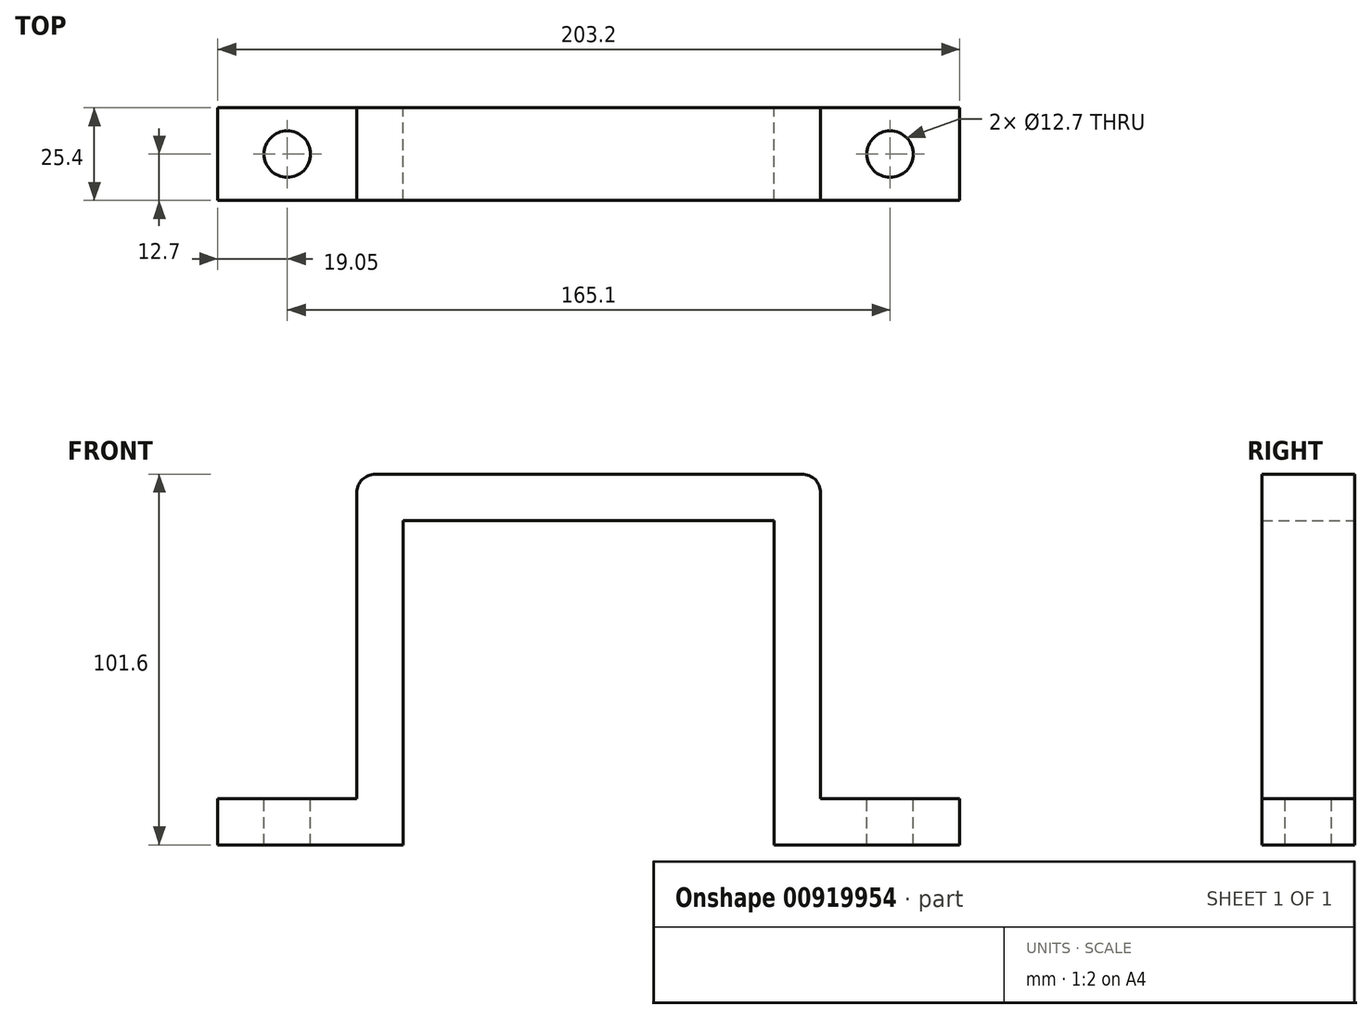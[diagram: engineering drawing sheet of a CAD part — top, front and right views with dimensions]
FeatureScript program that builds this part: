
annotation { "Feature Type Name" : "Feature", "Feature Type Description" : "" }
export const myFeature = defineFeature(function(context is Context, id is Id, definition is map)
    precondition{}
    {
        {
            var Q0;
            Q0=qCreatedBy(makeId("Top.planeOp"),FACE);
            var sketch = newSketch(context, id + "F0", { "sketchPlane" : qUnion([Q0])});
            skLineSegment(sketch, "E0.bottom", {"start": v(-63.5, 12.7) * mm, "end": v(63.5, 12.7) * mm});
            skLineSegment(sketch, "E0.top", {"start": v(-63.5, -12.7) * mm, "end": v(63.5, -12.7) * mm});
            skLineSegment(sketch, "E0.left", {"start": v(-63.5, 12.7) * mm, "end": v(-63.5, -12.7) * mm});
            skLineSegment(sketch, "E0.right", {"start": v(63.5, 12.7) * mm, "end": v(63.5, -12.7) * mm});
            skPoint(sketch, "E0.middle", {"position": v(0, 0) * mm});
            skSolve(sketch);
        }
        {
            var Q0;
            Q0 = qSketchRegion(id + "F0", true);
            extrude(context, id + "F1", {"entities" : qUnion([Q0]), "depth" : 12.7 * mm, "offsetDistance" : 25.4 * mm});
        }
        {
            var Q0;
            Q0=makeQuery(id+"F1.opExtrude","CAP_FACE",FACE,{"disambiguationData":[OSD([sQuery(id+"F0.wireOp",EDGE,"E0.bottom"),sQuery(id+"F0.wireOp",EDGE,"E0.top"),sQuery(id+"F0.wireOp",EDGE,"E0.left"),sQuery(id+"F0.wireOp",EDGE,"E0.right")])],"isStart":true});
            var sketch = newSketch(context, id + "F2", { "sketchPlane" : qUnion([Q0])});
            skLineSegment(sketch, "E1.bottom", {"start": v(63.5, 12.7) * mm, "end": v(50.8, 12.7) * mm});
            skLineSegment(sketch, "E1.top", {"start": v(63.5, -12.7) * mm, "end": v(50.8, -12.7) * mm});
            skLineSegment(sketch, "E1.left", {"start": v(63.5, 12.7) * mm, "end": v(63.5, -12.7) * mm});
            skLineSegment(sketch, "E1.right", {"start": v(50.8, 12.7) * mm, "end": v(50.8, -12.7) * mm});
            skSolve(sketch);
        }
        {
            var Q0;
            Q0 = qSketchRegion(id + "F2", true);
            extrude(context, id + "F3", {"entities" : qUnion([Q0]), "operationType" : NewBodyOperationType.ADD, "depth" : 76.2 * mm, "offsetDistance" : 25.4 * mm});
        }
        {
            var Q0;
            Q0=makeQuery(id+"F1.opExtrude","CAP_FACE",FACE,{"disambiguationData":[OSD([sQuery(id+"F0.wireOp",EDGE,"E0.bottom"),sQuery(id+"F0.wireOp",EDGE,"E0.top"),sQuery(id+"F0.wireOp",EDGE,"E0.left"),sQuery(id+"F0.wireOp",EDGE,"E0.right")])],"isStart":true});
            var sketch = newSketch(context, id + "F4", { "sketchPlane" : qUnion([Q0])});
            skLineSegment(sketch, "E2.bottom", {"start": v(-63.5, 12.7) * mm, "end": v(-50.8, 12.7) * mm});
            skLineSegment(sketch, "E2.top", {"start": v(-63.5, -12.7) * mm, "end": v(-50.8, -12.7) * mm});
            skLineSegment(sketch, "E2.left", {"start": v(-63.5, 12.7) * mm, "end": v(-63.5, -12.7) * mm});
            skLineSegment(sketch, "E2.right", {"start": v(-50.8, 12.7) * mm, "end": v(-50.8, -12.7) * mm});
            skSolve(sketch);
        }
        {
            var Q0;
            Q0 = qSketchRegion(id + "F4", true);
            extrude(context, id + "F5", {"entities" : qUnion([Q0]), "operationType" : NewBodyOperationType.ADD, "depth" : 76.2 * mm, "offsetDistance" : 25.4 * mm});
        }
        {
            var Q0;
            Q0=makeQuery(id+"F5.opExtrude","CAP_FACE",FACE,{"disambiguationData":[OSD([sQuery(id+"F4.wireOp",EDGE,"E2.bottom"),sQuery(id+"F4.wireOp",EDGE,"E2.top"),sQuery(id+"F4.wireOp",EDGE,"E2.left"),sQuery(id+"F4.wireOp",EDGE,"E2.right")])],"isStart":false});
            var sketch = newSketch(context, id + "F6", { "sketchPlane" : qUnion([Q0])});
            skLineSegment(sketch, "E3.bottom", {"start": v(-50.8, 12.7) * mm, "end": v(-101.6, 12.7) * mm});
            skLineSegment(sketch, "E3.top", {"start": v(-50.8, -12.7) * mm, "end": v(-101.6, -12.7) * mm});
            skLineSegment(sketch, "E3.left", {"start": v(-50.8, 12.7) * mm, "end": v(-50.8, -12.7) * mm});
            skLineSegment(sketch, "E3.right", {"start": v(-101.6, 12.7) * mm, "end": v(-101.6, -12.7) * mm});
            skSolve(sketch);
        }
        {
            var Q0;
            Q0 = qSketchRegion(id + "F6", true);
            extrude(context, id + "F7", {"entities" : qUnion([Q0]), "operationType" : NewBodyOperationType.ADD, "depth" : 12.7 * mm, "offsetDistance" : 25.4 * mm});
        }
        {
            var Q0;
            Q0=makeQuery(id+"F3.opExtrude","CAP_FACE",FACE,{"disambiguationData":[OSD([sQuery(id+"F2.wireOp",EDGE,"E1.bottom"),sQuery(id+"F2.wireOp",EDGE,"E1.top"),sQuery(id+"F2.wireOp",EDGE,"E1.left"),sQuery(id+"F2.wireOp",EDGE,"E1.right")])],"isStart":false});
            var sketch = newSketch(context, id + "F8", { "sketchPlane" : qUnion([Q0])});
            skLineSegment(sketch, "E4.bottom", {"start": v(50.8, 12.7) * mm, "end": v(101.6, 12.7) * mm});
            skLineSegment(sketch, "E4.top", {"start": v(50.8, -12.7) * mm, "end": v(101.6, -12.7) * mm});
            skLineSegment(sketch, "E4.left", {"start": v(50.8, 12.7) * mm, "end": v(50.8, -12.7) * mm});
            skLineSegment(sketch, "E4.right", {"start": v(101.6, 12.7) * mm, "end": v(101.6, -12.7) * mm});
            skSolve(sketch);
        }
        {
            var Q0;
            Q0 = qSketchRegion(id + "F8", true);
            extrude(context, id + "F9", {"entities" : qUnion([Q0]), "operationType" : NewBodyOperationType.ADD, "depth" : 12.7 * mm, "offsetDistance" : 25.4 * mm});
        }
        {
            var Q0;
            Q0=makeQuery(id+"F9.opExtrude","CAP_FACE",FACE,{"disambiguationData":[OSD([sQuery(id+"F8.wireOp",EDGE,"E4.bottom"),sQuery(id+"F8.wireOp",EDGE,"E4.top"),sQuery(id+"F8.wireOp",EDGE,"E4.left"),sQuery(id+"F8.wireOp",EDGE,"E4.right")])],"isStart":true});
            var sketch = newSketch(context, id + "F10", { "sketchPlane" : qUnion([Q0])});
            skLineSegment(sketch, "E5", {"start": v(101.6, 0) * mm, "end": v(63.5, 0) * mm});
            skCircle(sketch, "E6", {"center": v(82.55, 0) * mm, "radius": 6.35 * mm});
            skSolve(sketch);
        }
        {
            var Q0;
            Q0 = qSketchRegion(id + "F10", true);
            extrude(context, id + "F11", {"entities" : qUnion([Q0]), "operationType" : NewBodyOperationType.REMOVE, "oppositeDirection" : true, "depth" : 25.4 * mm, "offsetDistance" : 25.4 * mm});
        }
        {
            var Q0;
            Q0=makeQuery(id+"F7.opExtrude","CAP_FACE",FACE,{"disambiguationData":[OSD([sQuery(id+"F6.wireOp",EDGE,"E3.bottom"),sQuery(id+"F6.wireOp",EDGE,"E3.top"),sQuery(id+"F6.wireOp",EDGE,"E3.left"),sQuery(id+"F6.wireOp",EDGE,"E3.right")])],"isStart":true});
            var sketch = newSketch(context, id + "F12", { "sketchPlane" : qUnion([Q0])});
            skLineSegment(sketch, "E7", {"start": v(-101.6, 0) * mm, "end": v(-63.5, 0) * mm});
            skCircle(sketch, "E8", {"center": v(-82.55, 0) * mm, "radius": 6.35 * mm});
            skSolve(sketch);
        }
        {
            var Q0;
            Q0 = qSketchRegion(id + "F12", true);
            extrude(context, id + "F13", {"entities" : qUnion([Q0]), "operationType" : NewBodyOperationType.REMOVE, "oppositeDirection" : true, "depth" : 25.4 * mm, "offsetDistance" : 25.4 * mm});
        }
        {
            var Q0;
            Q0=makeQuery(id+"F1.opExtrude","CAP_EDGE",EDGE,{"disambiguationData":[OSD([sQuery(id+"F0.wireOp",EDGE,"E0.right")])],"isStart":false});
            fillet(context, id + "F14", {"entities" : qUnion([Q0]), "radius" : 5.08 * mm, "tangentPropagation" : true, "allowEdgeOverflow" : false});
        }
        {
            var Q0;
            Q0=makeQuery(id+"F1.opExtrude","CAP_EDGE",EDGE,{"disambiguationData":[OSD([sQuery(id+"F0.wireOp",EDGE,"E0.left")])],"isStart":false});
            fillet(context, id + "F15", {"entities" : qUnion([Q0]), "radius" : 5.08 * mm, "tangentPropagation" : true, "allowEdgeOverflow" : false});
        }
    });
